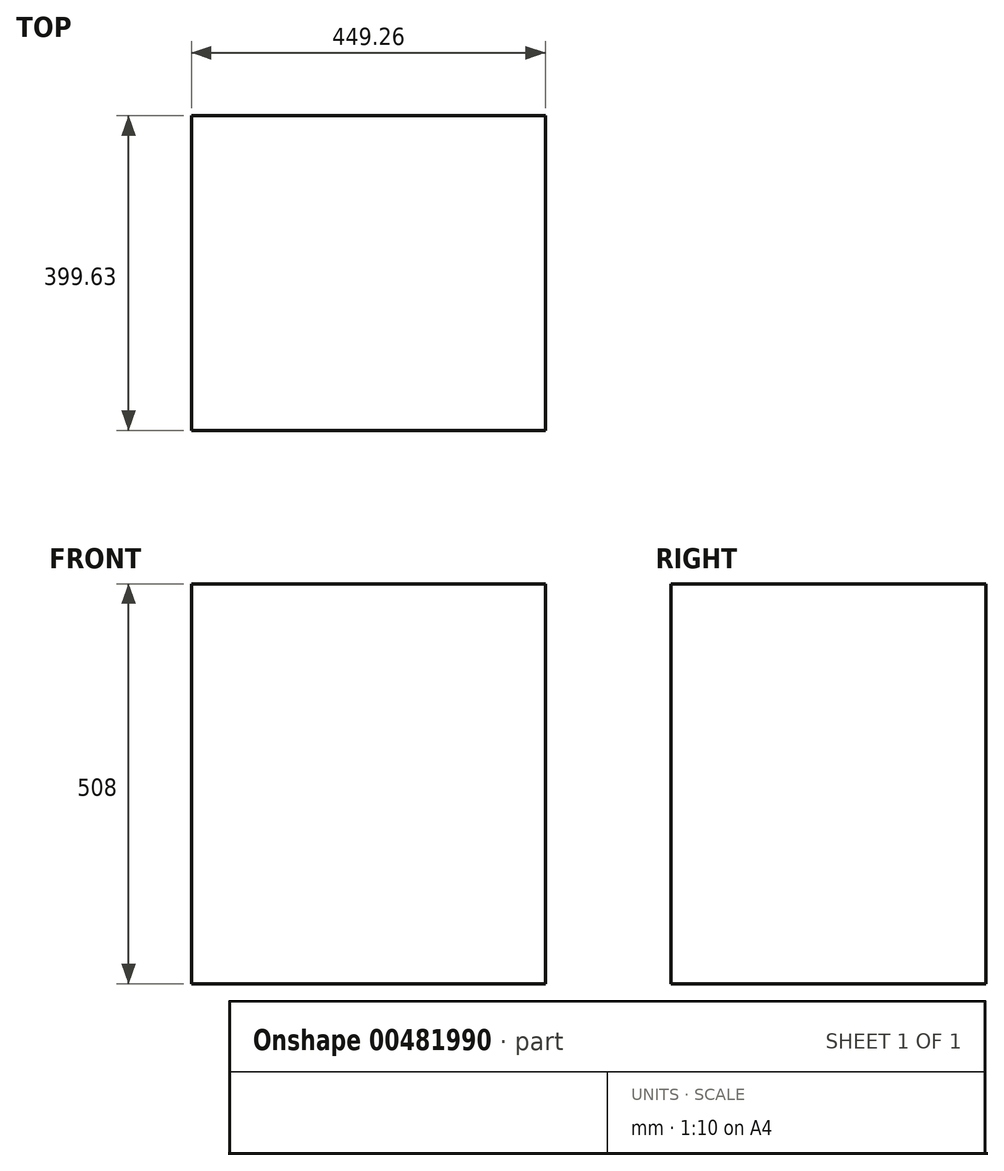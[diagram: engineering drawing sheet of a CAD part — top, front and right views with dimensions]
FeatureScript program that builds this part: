
annotation { "Feature Type Name" : "Feature", "Feature Type Description" : "" }
export const myFeature = defineFeature(function(context is Context, id is Id, definition is map)
    precondition{}
    {
        {
            var Q0;
            Q0=qCreatedBy(makeId("Top.planeOp"),FACE);
            var sketch = newSketch(context, id + "F0", { "sketchPlane" : qUnion([Q0])});
            skLineSegment(sketch, "E0.bottom", {"start": v(24.07, 64.29) * mm, "end": v(-176.35, 64.29) * mm});
            skLineSegment(sketch, "E0.top", {"start": v(24.07, 104.7) * mm, "end": v(-176.35, 104.7) * mm});
            skLineSegment(sketch, "E0.left", {"start": v(24.07, 104.7) * mm, "end": v(24.07, 64.29) * mm});
            skLineSegment(sketch, "E0.right", {"start": v(-176.35, 104.7) * mm, "end": v(-176.35, 64.29) * mm});
            skSolve(sketch);
        }
        {
            var Q0;
            Q0=makeQuery(id+"F0.imprint","IMPRINT",FACE,{"disambiguationData":[TD([[makeQuery(id+"F0.imprint","IMPRINT",EDGE,{"derivedFrom":sQuery(id+"F0.wireOp",EDGE,"E0.bottom")}),-1.0]])]});
            var sketch = newSketch(context, id + "F1", { "sketchPlane" : qUnion([Q0])});
            skLineSegment(sketch, "E1.bottom", {"start": v(-296.67, 0) * mm, "end": v(152.6, 0) * mm});
            skLineSegment(sketch, "E1.top", {"start": v(-296.67, -145.63) * mm, "end": v(152.6, -145.63) * mm});
            skLineSegment(sketch, "E1.left", {"start": v(-296.67, 0) * mm, "end": v(-296.67, -145.63) * mm});
            skLineSegment(sketch, "E1.right", {"start": v(152.6, 0) * mm, "end": v(152.6, -145.63) * mm});
            skLineSegment(sketch, "E2.bottom", {"start": v(53.25, 95.22) * mm, "end": v(-97.5, 95.22) * mm});
            skLineSegment(sketch, "E2.top", {"start": v(53.25, 88.73) * mm, "end": v(-97.5, 88.73) * mm});
            skLineSegment(sketch, "E2.left", {"start": v(53.25, 95.22) * mm, "end": v(53.25, 88.73) * mm});
            skLineSegment(sketch, "E2.right", {"start": v(-97.5, 95.22) * mm, "end": v(-97.5, 88.73) * mm});
            skSolve(sketch);
        }
        {
            var Q0;
            Q0=makeQuery(id+"F1.imprint","IMPRINT",FACE,{"disambiguationData":[TD([[makeQuery(id+"F1.imprint","IMPRINT",EDGE,{"derivedFrom":sQuery(id+"F1.wireOp",EDGE,"E1.bottom")}),-1.0]])]});
            extrude(context, id + "F2", {"entities" : qUnion([Q0]), "depth" : 508 * mm});
        }
        {
            var Q0;
            Q0=makeQuery(id+"F2.opExtrude","SWEPT_FACE",FACE,{"disambiguationData":[OSD([sQuery(id+"F1.wireOp",EDGE,"E1.top")])]});
            extrude(context, id + "F3", {"entities" : qUnion([Q0]), "operationType" : NewBodyOperationType.ADD, "depth" : 254 * mm});
        }
        {
            var Q0;
            Q0=makeQuery(id+"F3.opExtrude","CAP_FACE",FACE,{"disambiguationData":[OSD([sQuery(id+"F1.wireOp",EDGE,"E1.top")])],"isStart":false});
            extrude(context, id + "F4", {"entities" : qUnion([Q0]), "operationType" : NewBodyOperationType.ADD, "depth" : -127 * mm});
        }
        {
            var Q0;
            Q0=makeQuery(id+"F3.opExtrude","CAP_FACE",FACE,{"disambiguationData":[OSD([sQuery(id+"F1.wireOp",EDGE,"E1.top")])],"isStart":false});
            extrude(context, id + "F5", {"entities" : qUnion([Q0]), "operationType" : NewBodyOperationType.ADD, "depth" : -127 * mm});
        }
    });
